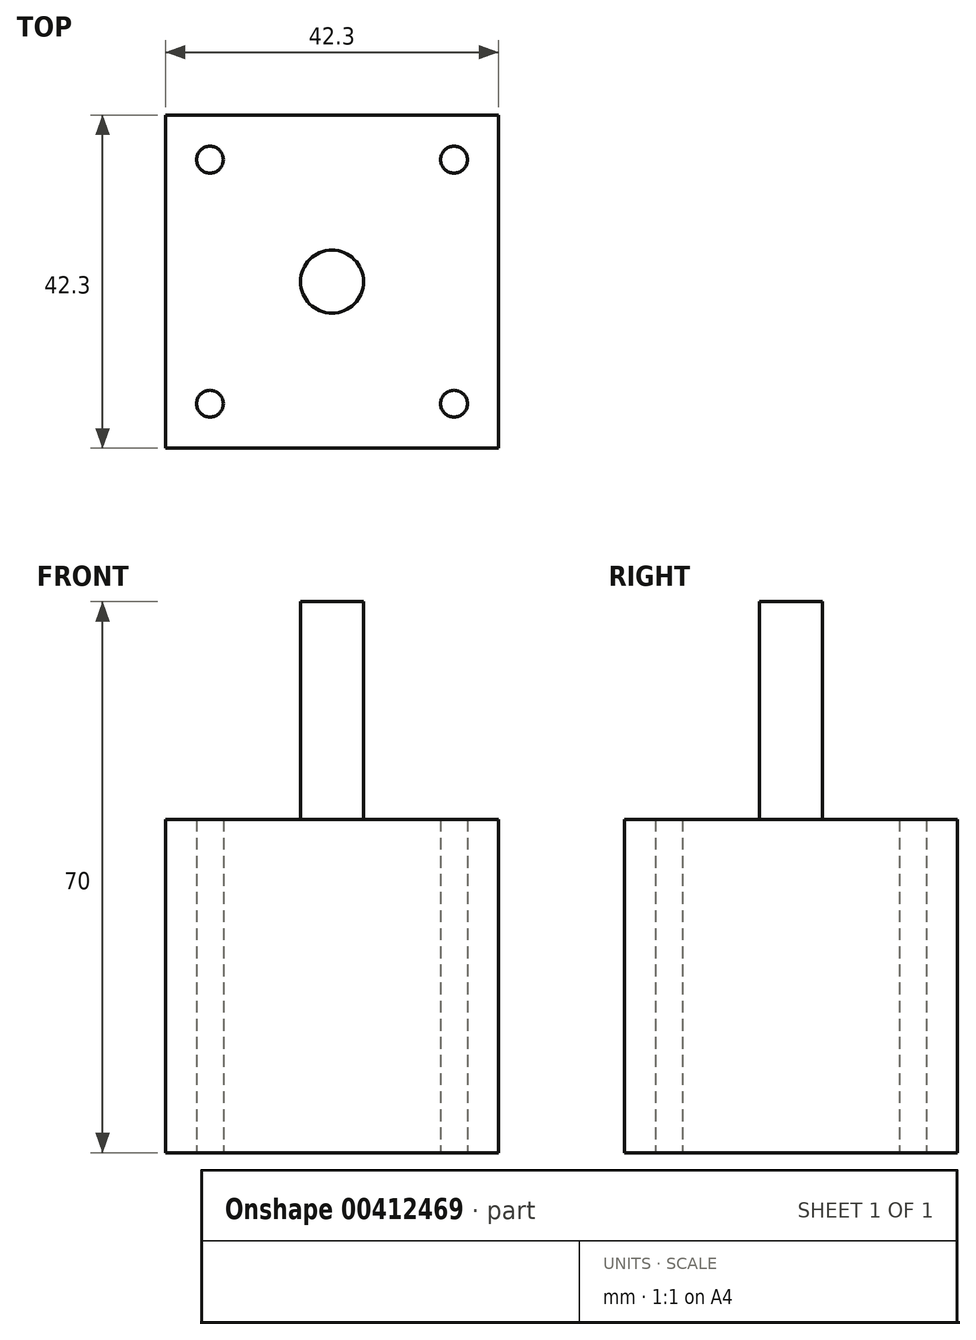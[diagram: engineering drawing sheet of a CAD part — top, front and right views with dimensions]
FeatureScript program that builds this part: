
annotation { "Feature Type Name" : "Feature", "Feature Type Description" : "" }
export const myFeature = defineFeature(function(context is Context, id is Id, definition is map)
    precondition{}
    {
        {
            var Q0;
            Q0=qCreatedBy(makeId("Top.planeOp"),FACE);
            var sketch = newSketch(context, id + "F0", { "sketchPlane" : qUnion([Q0])});
            skLineSegment(sketch, "E0.bottom", {"start": v(21.15, 21.15) * mm, "end": v(-21.15, 21.15) * mm});
            skLineSegment(sketch, "E0.top", {"start": v(21.15, -21.15) * mm, "end": v(-21.15, -21.15) * mm});
            skLineSegment(sketch, "E0.left", {"start": v(21.15, 21.15) * mm, "end": v(21.15, -21.15) * mm});
            skLineSegment(sketch, "E0.right", {"start": v(-21.15, 21.15) * mm, "end": v(-21.15, -21.15) * mm});
            skPoint(sketch, "E0.middle", {"position": v(0, 0) * mm});
            skCircle(sketch, "E1", {"center": v(0, 0) * mm, "radius": 4 * mm});
            skLineSegment(sketch, "E2.bottom", {"start": v(-15.5, 15.5) * mm, "end": v(15.5, 15.5) * mm});
            skLineSegment(sketch, "E2.top", {"start": v(-15.5, -15.5) * mm, "end": v(15.5, -15.5) * mm});
            skLineSegment(sketch, "E2.left", {"start": v(-15.5, 15.5) * mm, "end": v(-15.5, -15.5) * mm});
            skLineSegment(sketch, "E2.right", {"start": v(15.5, 15.5) * mm, "end": v(15.5, -15.5) * mm});
            skCircle(sketch, "E3", {"center": v(-15.5, -15.5) * mm, "radius": 1.5 * mm});
            skCircle(sketch, "E4", {"center": v(-15.5, 15.5) * mm, "radius": 1.5 * mm});
            skCircle(sketch, "E5", {"center": v(15.5, 15.5) * mm, "radius": 1.5 * mm});
            skCircle(sketch, "E6", {"center": v(15.5, -15.5) * mm, "radius": 1.5 * mm});
            skCircle(sketch, "E7.0", {"center": v(-15.5, 15.5) * mm, "radius": 1.7 * mm});
            skCircle(sketch, "E8.0", {"center": v(15.5, 15.5) * mm, "radius": 1.7 * mm});
            skCircle(sketch, "E9.0", {"center": v(15.5, -15.5) * mm, "radius": 1.7 * mm});
            skCircle(sketch, "E10.0", {"center": v(-15.5, -15.5) * mm, "radius": 1.7 * mm});
            skSolve(sketch);
        }
        {
            var Q0;
            Q0=makeQuery(id+"F0.imprint","IMPRINT",FACE,{"disambiguationData":[TD([[makeQuery(id+"F0.imprint","IMPRINT",EDGE,{"derivedFrom":sQuery(id+"F0.wireOp",EDGE,"E0.bottom")}),1.0]])]});
            var Q1;
            Q1=makeQuery(id+"F0.imprint","IMPRINT",FACE,{"disambiguationData":[TD([[makeQuery(id+"F0.imprint","IMPRINT",EDGE,{"derivedFrom":sQuery(id+"F0.wireOp",EDGE,"E1")}),-1.0]])]});
            var Q2;
            Q2=makeQuery(id+"F0.imprint","IMPRINT",FACE,{"disambiguationData":[TD([[makeQuery(id+"F0.imprint","IMPRINT",EDGE,{"derivedFrom":sQuery(id+"F0.wireOp",EDGE,"E1")}),1.0]])]});
            extrude(context, id + "F1", {"entities" : qUnion([Q0, Q1, Q2]), "depth" : 42.3 * mm});
        }
        {
            var Q0;
            Q0=makeQuery(id+"F0.imprint","IMPRINT",FACE,{"disambiguationData":[TD([[makeQuery(id+"F0.imprint","IMPRINT",EDGE,{"derivedFrom":sQuery(id+"F0.wireOp",EDGE,"E1")}),1.0]])]});
            extrude(context, id + "F2", {"entities" : qUnion([Q0]), "operationType" : NewBodyOperationType.ADD, "depth" : 70 * mm});
        }
    });
